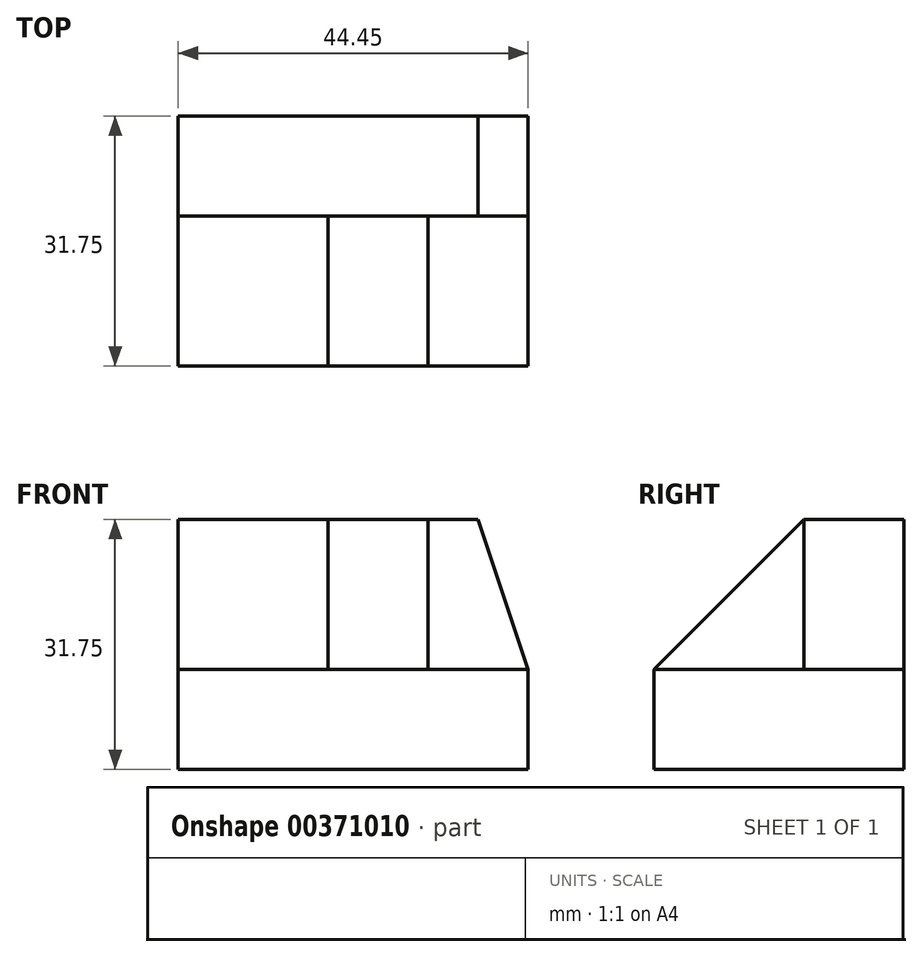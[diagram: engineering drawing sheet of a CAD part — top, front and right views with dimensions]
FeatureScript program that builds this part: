
annotation { "Feature Type Name" : "Feature", "Feature Type Description" : "" }
export const myFeature = defineFeature(function(context is Context, id is Id, definition is map)
    precondition{}
    {
        {
            var Q0;
            Q0=qCreatedBy(makeId("Front.planeOp"),FACE);
            var sketch = newSketch(context, id + "F0", { "sketchPlane" : qUnion([Q0])});
            skLineSegment(sketch, "E0", {"start": v(0, 0) * mm, "end": v(-44.45, 0) * mm});
            skLineSegment(sketch, "E1", {"start": v(-44.45, 0) * mm, "end": v(-44.45, 12.7) * mm});
            skLineSegment(sketch, "E2", {"start": v(-44.45, 12.7) * mm, "end": v(0, 12.7) * mm});
            skLineSegment(sketch, "E3", {"start": v(0, 0) * mm, "end": v(0, 12.7) * mm});
            skSolve(sketch);
        }
        {
            var Q0;
            Q0 = qSketchRegion(id + "F0", true);
            extrude(context, id + "F1", {"entities" : qUnion([Q0]), "depth" : 31.75 * mm});
        }
        {
            var Q0;
            Q0=makeQuery(id+"F1.opExtrude","SWEPT_FACE",FACE,{"disambiguationData":[OSD([sQuery(id+"F0.wireOp",EDGE,"E2")])]});
            var sketch = newSketch(context, id + "F2", { "sketchPlane" : qUnion([Q0])});
            skLineSegment(sketch, "E4", {"start": v(0, 0) * mm, "end": v(0, -12.7) * mm});
            skLineSegment(sketch, "E5", {"start": v(0, -12.7) * mm, "end": v(-44.45, -12.7) * mm});
            skSolve(sketch);
        }
        {
            var Q0;
            Q0 = qSketchRegion(id + "F2", true);
            var Q1;
            Q1=makeQuery(id+"F2.imprint","IMPRINT",FACE,{"disambiguationData":[TD([[makeQuery(id+"F2.imprint","IMPRINT",EDGE,{"derivedFrom":sQuery(id+"F2.wireOp",EDGE,"E4")}),1.0]])]});
            extrude(context, id + "F3", {"entities" : qUnion([Q0, Q1]), "operationType" : NewBodyOperationType.ADD, "depth" : 19.05 * mm});
        }
        {
            var Q0;
            Q0=makeQuery(id+"F3.opExtrude","SWEPT_FACE",FACE,{"disambiguationData":[OSD([sQuery(id+"F2.wireOp",EDGE,"E5")])]});
            var sketch = newSketch(context, id + "F4", { "sketchPlane" : qUnion([Q0])});
            skLineSegment(sketch, "E6", {"start": v(-44.45, 31.75) * mm, "end": v(-25.4, 31.75) * mm});
            skLineSegment(sketch, "E7", {"start": v(-25.4, 31.75) * mm, "end": v(-25.4, 12.7) * mm});
            skLineSegment(sketch, "E8", {"start": v(-25.4, 12.7) * mm, "end": v(-12.7, 12.7) * mm});
            skLineSegment(sketch, "E9", {"start": v(-12.7, 12.7) * mm, "end": v(-12.7, 31.75) * mm});
            skSolve(sketch);
        }
        {
            var Q0;
            Q0 = qSketchRegion(id + "F4", true);
            var Q1;
            {var subQ0=sQuery(id+"F4.wireOp",EDGE,"E7");Q1=makeQuery(id+"F4.imprint","IMPRINT",FACE,{"disambiguationData":[TD([[makeQuery(id+"F4.imprint","IMPRINT",EDGE,{"derivedFrom":subQ0}),1.0]])]});}
            extrude(context, id + "F5", {"entities" : qUnion([Q0, Q1]), "operationType" : NewBodyOperationType.ADD, "depth" : 19.05 * mm});
        }
        {
            var Q0;
            Q0=makeQuery(id+"F5.opExtrude","SWEPT_FACE",FACE,{"disambiguationData":[OSD([sQuery(id+"F4.wireOp",EDGE,"E9")])]});
            var sketch = newSketch(context, id + "F6", { "sketchPlane" : qUnion([Q0])});
            skLineSegment(sketch, "E10", {"start": v(-31.75, 12.7) * mm, "end": v(-12.7, 31.75) * mm});
            skSolve(sketch);
        }
        {
            var Q0;
            Q0 = qSketchRegion(id + "F6", true);
            var Q1;
            Q1=makeQuery(id+"F6.imprint","IMPRINT",FACE,{"disambiguationData":[TD([[makeQuery(id+"F6.imprint","IMPRINT",EDGE,{"derivedFrom":sQuery(id+"F6.wireOp",EDGE,"E10")}),1.0]])]});
            extrude(context, id + "F7", {"entities" : qUnion([Q0, Q1]), "operationType" : NewBodyOperationType.REMOVE, "oppositeDirection" : true, "depth" : 25.4 * mm});
        }
        {
            var Q0;
            {var subQ1=sQuery(id+"F2.wireOp",EDGE,"E5");Q0=makeQuery(id+"F5.boolean.opBoolean","SPLIT",FACE,{"disambiguationData":[TD([makeQuery(id+"F1.opExtrude","SWEPT_FACE",FACE,{"disambiguationData":[OSD([sQuery(id+"F0.wireOp",EDGE,"E3")])]})])],"derivedFrom":makeQuery(id+"F3.opExtrude","SWEPT_FACE",FACE,{"disambiguationData":[OSD([subQ1])]})});}
            var sketch = newSketch(context, id + "F8", { "sketchPlane" : qUnion([Q0])});
            skLineSegment(sketch, "E11", {"start": v(-12.7, 31.75) * mm, "end": v(-6.35, 31.75) * mm});
            skLineSegment(sketch, "E12", {"start": v(-6.35, 31.75) * mm, "end": v(0, 12.7) * mm});
            skSolve(sketch);
        }
        {
            var Q0;
            Q0 = qSketchRegion(id + "F8", true);
            var Q1;
            {var subQ0=sQuery(id+"F8.wireOp",EDGE,"E12");Q1=makeQuery(id+"F8.imprint","IMPRINT",FACE,{"disambiguationData":[TD([[makeQuery(id+"F8.imprint","IMPRINT",EDGE,{"derivedFrom":subQ0}),1.0]])]});}
            extrude(context, id + "F9", {"entities" : qUnion([Q0, Q1]), "operationType" : NewBodyOperationType.REMOVE, "oppositeDirection" : true, "depth" : 25.4 * mm});
        }
    });
